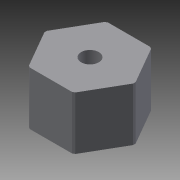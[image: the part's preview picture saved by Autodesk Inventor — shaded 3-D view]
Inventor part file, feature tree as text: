
AUTODESK INVENTOR PART (.ipt)
format: ipt  version: 2013 (Build 170138000, 138)  size: 227,840 bytes
history: native  units: mm
features: sketch x7, extrude x6, helix x1, projected_geometry x1
ambient origin geometry x8: Origin, YZ Plane, XZ Plane, XY Plane, X Axis, Y Axis, Z Axis, Center Point
bodies: Solid1 (feature_tree)
feature tree (15):
  extrude  "Extrusion1"  Depth=15.0mm TaperAngle=0.0deg
  extrude  "Extrusion2"  Depth=15.0mm TaperAngle=0.0deg
  helix  "Coil1"  [1 undecoded]
  extrude  "Extrusion8"  Depth=5.0mm TaperAngle=0.0deg
  extrude  "Extrusion9"  Depth=5.0mm
  extrude  "Extrusion10"  Depth=22.0mm
  extrude  "Extrusion11"  [1 undecoded]
  sketch  "Sketch1"  dims[d0=25.0mm d2=15.0mm d3=0.0mm]
  sketch  "Sketch2"  dims[d4=13.9mm d9=15.0mm d10=0.0mm d11=2.0mm]
  sketch  "Sketch3"  dims[d12=2.0001mm d13=10.0mm d14=100.0mm d15=0.0mm d16=90.0deg d17=90.0deg d18=0.0mm d19=0.0mm d47=5.0mm d48=0.0mm]
  sketch  "Sketch9"  dims[d49=5.0mm d50=-7.853982mm d51=5.0mm]
  sketch  "Sketch10"  dims[d53=5.0mm d54=0.0mm d55=22.0mm]
  sketch  "Sketch11"  dims[d56=0.0mm d57=0.0mm]
  sketch  "Sketch12"
  projected_geometry  "Project Cut Edges1"
note: 2 required parameter values undecoded (feature->parameter linkage not recoverable at this tier; creation-order binding heuristic only, values carry confidence <= 0.55)
